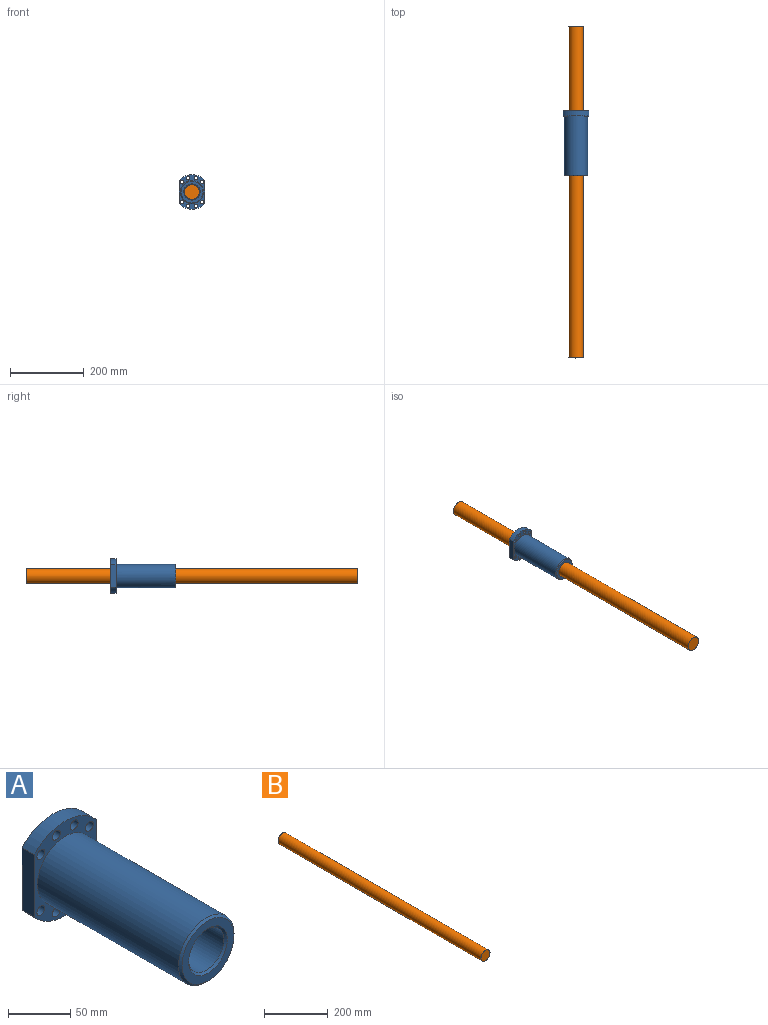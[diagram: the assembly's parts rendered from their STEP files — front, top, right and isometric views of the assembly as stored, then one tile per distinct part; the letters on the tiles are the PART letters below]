
ASSEMBLY  parts=2 mates=1
PART A: 21 faces, bbox 70x176x93 mm
  f0: cylinder r=20mm len=172mm, axis (0,-1,0), area 21577.7mm2, adj f17,f18,f19
  f1: plane 61.23x14mm, normal (-1,0,0), area 857.2mm2, adj f2,f5,f13,f14
  f2: cylinder r=46.5mm len=70mm, axis (0,-1,0), area 1109.5mm2, adj f1,f3,f13,f14
  f3: plane 61.23x14mm, normal (1,0,0), area 820.9mm2, adj f2,f5,f13,f14,f17
  f4: cylinder r=4.5mm len=14mm, axis (0,-1,0), area 395.8mm2, adj f13,f14
  f5: cylinder r=46.5mm len=70mm, axis (0,-1,0), area 1109.5mm2, adj f1,f3,f13,f14
  f6: cylinder r=4.5mm len=14mm, axis (0,-1,0), area 395.8mm2, adj f13,f14
  f7: cylinder r=4.5mm len=14mm, axis (0,-1,0), area 395.8mm2, adj f13,f14
  f8: cylinder r=4.5mm len=14mm, axis (0,-1,0), area 395.8mm2, adj f13,f14
  f9: cylinder r=4.5mm len=14mm, axis (0,-1,0), area 395.8mm2, adj f13,f14
  f10: cylinder r=4.5mm len=14mm, axis (0,-1,0), area 395.8mm2, adj f13,f14
  f11: cylinder r=4.5mm len=14mm, axis (0,-1,0), area 395.8mm2, adj f13,f14
  f12: cylinder r=4.5mm len=14mm, axis (0,-1,0), area 395.8mm2, adj f13,f14
  f13: plane 93x70mm, normal (0,1,0), area 3798.6mm2, adj f1,f2,f3,f4,f5,f6,f7,f8
  f14: plane 93x70mm, normal (0,-1,0), area 2201.9mm2, adj f1,f2,f3,f4,f5,f6,f7,f8
  f15: cylinder r=31.5mm len=160mm, axis (0,1,0), area 31667.3mm2, adj f14,f20
  f16: plane 59x59mm, normal (0,-1,0), area 1213.4mm2, adj f18,f20
  f17: cylinder r=3.4mm len=15.29mm, axis (1,0,0), area 323.6mm2, adj f0,f3
  f18: cone r=20mm half-angle=45deg, axis (0,-1,0), area 373.2mm2, adj f0,f16
  f19: cone r=22mm half-angle=45deg, axis (0,1,0), area 373.2mm2, adj f0,f13
  f20: cone r=29.5mm half-angle=45deg, axis (0,1,0), area 542mm2, adj f15,f16
PART B: 3 faces, bbox 40x900x40 mm
  f0: cylinder r=20mm len=900mm, axis (0,1,0), area 113097.3mm2, adj f1,f2
  f1: plane 40x40mm, normal (0,-1,0), area 1256.6mm2, adj f0
  f2: plane 40x40mm, normal (0,1,0), area 1256.6mm2, adj f0
PLACE A t=(-246.38,113.23,-141.79)mm
PLACE B t=(-246.38,107.23,-141.79)mm fixed
MATE fastened B.f0 <-> A.f0  axis (0,1,0) through (-246.38,107.23,-141.79)mm
